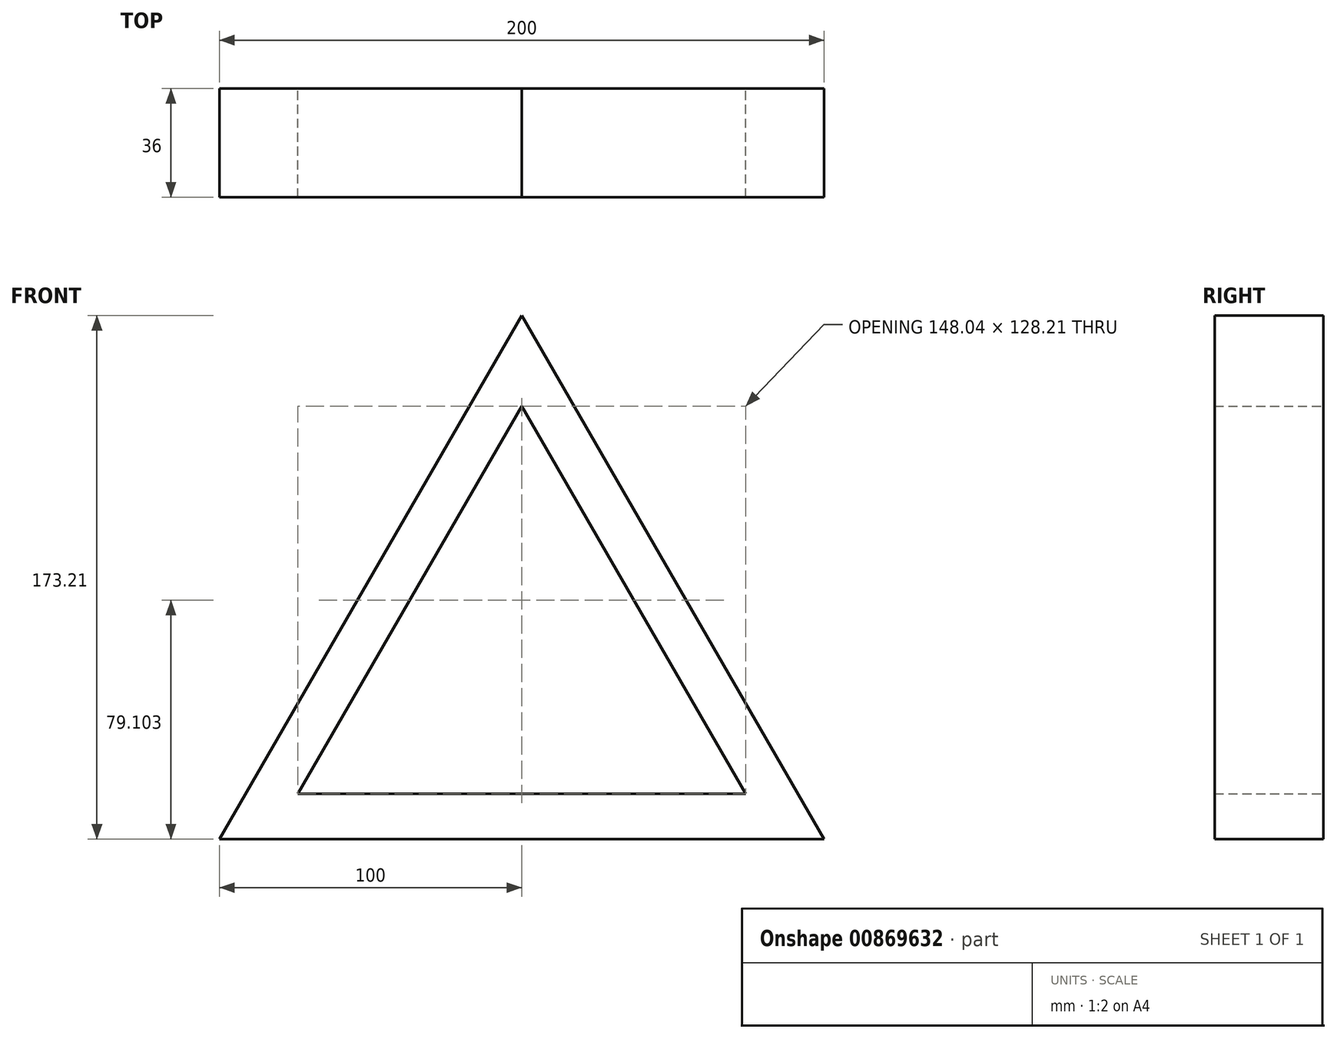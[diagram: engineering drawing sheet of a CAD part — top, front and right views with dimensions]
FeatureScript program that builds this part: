
annotation { "Feature Type Name" : "Feature", "Feature Type Description" : "" }
export const myFeature = defineFeature(function(context is Context, id is Id, definition is map)
    precondition{}
    {
        {
            var Q0;
            Q0=qCreatedBy(makeId("Front.planeOp"),FACE);
            var sketch = newSketch(context, id + "F0", { "sketchPlane" : qUnion([Q0])});
            skLineSegment(sketch, "E0", {"start": v(0, 0) * mm, "end": v(-100, 0) * mm});
            skLineSegment(sketch, "E1", {"start": v(0, 0) * mm, "end": v(0, 173.2) * mm});
            skLineSegment(sketch, "E2", {"start": v(0, 173.2) * mm, "end": v(-100, 0) * mm});
            skLineSegment(sketch, "E3.0", {"start": v(0, 15) * mm, "end": v(-74.02, 15) * mm});
            skLineSegment(sketch, "E3.1", {"start": v(0, 143.2) * mm, "end": v(-74.02, 15) * mm});
            skLineSegment(sketch, "E4.MirrorCS", {"start": v(0, 143.2) * mm, "end": v(74.02, 15) * mm});
            skLineSegment(sketch, "E5.MirrorCS", {"start": v(0, 173.2) * mm, "end": v(100, 0) * mm});
            skLineSegment(sketch, "E6.MirrorCS", {"start": v(0, 0) * mm, "end": v(100, 0) * mm});
            skLineSegment(sketch, "E7.MirrorCS", {"start": v(0, 15) * mm, "end": v(74.02, 15) * mm});
            skLineSegment(sketch, "E8", {"start": v(-100, 0) * mm, "end": v(-74.02, 15) * mm});
            skSolve(sketch);
        }
        {
            var Q0;
            {var subQ3=sQuery(id+"F0.wireOp",EDGE,"E0");Q0=makeQuery(id+"F0.imprint","IMPRINT",FACE,{"disambiguationData":[TD([[makeQuery(id+"F0.imprint","IMPRINT",EDGE,{"derivedFrom":subQ3}),-1.0]])]});}
            var Q1;
            {var subQ0=sQuery(id+"F0.wireOp",EDGE,"E4.MirrorCS");Q1=makeQuery(id+"F0.imprint","IMPRINT",FACE,{"disambiguationData":[TD([[makeQuery(id+"F0.imprint","IMPRINT",EDGE,{"derivedFrom":subQ0}),1.0]])]});}
            var Q2;
            {var subQ0=sQuery(id+"F0.wireOp",EDGE,"E2");Q2=makeQuery(id+"F0.imprint","IMPRINT",FACE,{"disambiguationData":[TD([[makeQuery(id+"F0.imprint","IMPRINT",EDGE,{"derivedFrom":subQ0}),1.0]])]});}
            extrude(context, id + "F1", {"entities" : qUnion([Q0, Q1, Q2]), "depth" : 36 * mm, "offsetDistance" : 25 * mm});
        }
    });
